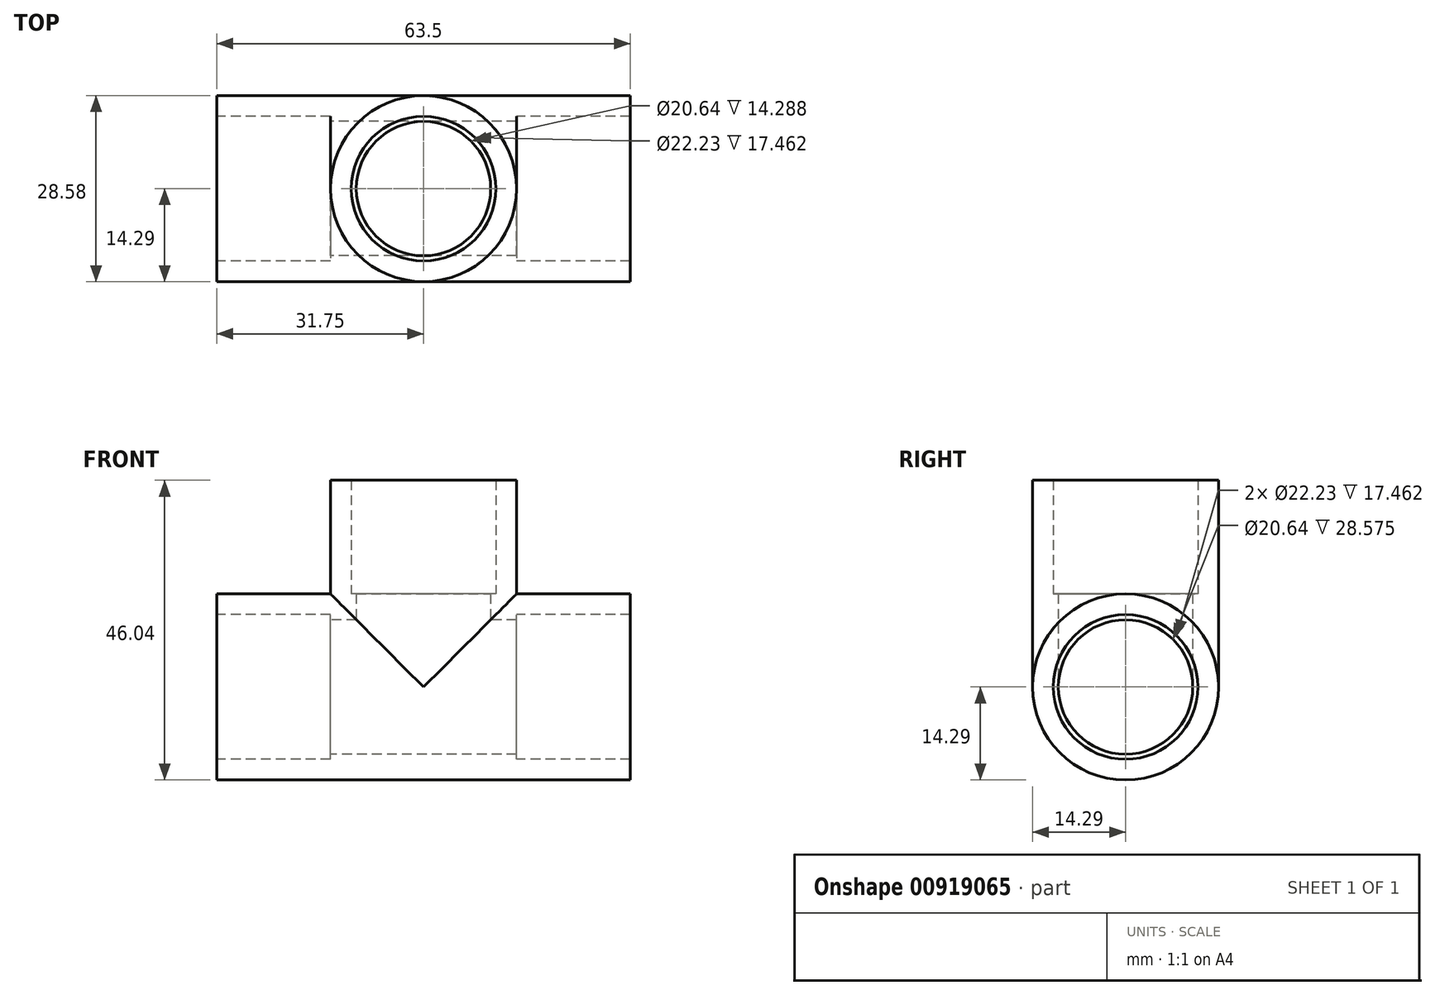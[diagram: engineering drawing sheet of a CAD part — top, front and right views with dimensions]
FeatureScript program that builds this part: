
annotation { "Feature Type Name" : "Feature", "Feature Type Description" : "" }
export const myFeature = defineFeature(function(context is Context, id is Id, definition is map)
    precondition{}
    {
        {
            var Q0;
            Q0=qCreatedBy(makeId("Top.planeOp"),FACE);
            var sketch = newSketch(context, id + "F0", { "sketchPlane" : qUnion([Q0])});
            skCircle(sketch, "E0", {"center": v(0, 0) * mm, "radius": 14.29 * mm});
            skCircle(sketch, "E1", {"center": v(0, 0) * mm, "radius": 11.11 * mm});
            skCircle(sketch, "E2", {"center": v(0, 0) * mm, "radius": 10.32 * mm});
            skSolve(sketch);
        }
        {
            var Q0;
            Q0 = qSketchRegion(id + "F0", true);
            extrude(context, id + "F1", {"entities" : qUnion([Q0]), "depth" : 31.75 * mm, "offsetDistance" : 25.4 * mm});
        }
        {
            var Q0;
            Q0=makeQuery(id+"F0.imprint","IMPRINT",FACE,{"disambiguationData":[TD([[makeQuery(id+"F0.imprint","IMPRINT",EDGE,{"derivedFrom":sQuery(id+"F0.wireOp",EDGE,"E1")}),1.0]])]});
            extrude(context, id + "F2", {"entities" : qUnion([Q0]), "operationType" : NewBodyOperationType.ADD, "depth" : 14.29 * mm, "offsetDistance" : 25.4 * mm});
        }
        {
            var Q0;
            Q0=qCreatedBy(makeId("Right.planeOp"),FACE);
            var sketch = newSketch(context, id + "F3", { "sketchPlane" : qUnion([Q0])});
            skCircle(sketch, "E3", {"center": v(0, 0) * mm, "radius": 14.29 * mm});
            skCircle(sketch, "E4", {"center": v(0, 0) * mm, "radius": 11.11 * mm});
            skCircle(sketch, "E5", {"center": v(0, 0) * mm, "radius": 10.32 * mm});
            skSolve(sketch);
        }
        {
            var Q0;
            Q0=makeQuery(id+"F3.imprint","IMPRINT",FACE,{"disambiguationData":[TD([[makeQuery(id+"F3.imprint","IMPRINT",EDGE,{"derivedFrom":sQuery(id+"F3.wireOp",EDGE,"E3")}),1.0]])]});
            var Q1;
            Q1=sQuery(id+"F3.wireOp",EDGE,"E3");
            var Q2;
            Q2=sQuery(id+"F3.wireOp",EDGE,"E4");
            extrude(context, id + "F4", {"entities" : qUnion([Q0]), "operationType" : NewBodyOperationType.ADD, "surfaceEntities" : qUnion([Q1, Q2]), "endBound" : BoundingType.SYMMETRIC, "depth" : 63.5 * mm, "offsetDistance" : 25.4 * mm});
        }
        {
            var Q0;
            Q0=makeQuery(id+"F3.imprint","IMPRINT",FACE,{"disambiguationData":[TD([[makeQuery(id+"F3.imprint","IMPRINT",EDGE,{"derivedFrom":sQuery(id+"F3.wireOp",EDGE,"E4")}),1.0]])]});
            extrude(context, id + "F5", {"entities" : qUnion([Q0]), "operationType" : NewBodyOperationType.ADD, "endBound" : BoundingType.SYMMETRIC, "depth" : 28.57 * mm, "offsetDistance" : 25.4 * mm});
        }
        {
            var Q0;
            Q0=makeQuery(id+"F3.imprint","IMPRINT",FACE,{"disambiguationData":[TD([[makeQuery(id+"F3.imprint","IMPRINT",EDGE,{"derivedFrom":sQuery(id+"F3.wireOp",EDGE,"E5")}),1.0]])]});
            extrude(context, id + "F6", {"entities" : qUnion([Q0]), "operationType" : NewBodyOperationType.REMOVE, "endBound" : BoundingType.SYMMETRIC, "oppositeDirection" : true, "depth" : 28.57 * mm, "offsetDistance" : 25.4 * mm});
        }
        {
            var Q0;
            Q0=makeQuery(id+"F0.imprint","IMPRINT",FACE,{"disambiguationData":[TD([[makeQuery(id+"F0.imprint","IMPRINT",EDGE,{"derivedFrom":sQuery(id+"F0.wireOp",EDGE,"E2")}),1.0]])]});
            extrude(context, id + "F7", {"entities" : qUnion([Q0]), "operationType" : NewBodyOperationType.REMOVE, "depth" : 14.29 * mm, "offsetDistance" : 25.4 * mm});
        }
    });
